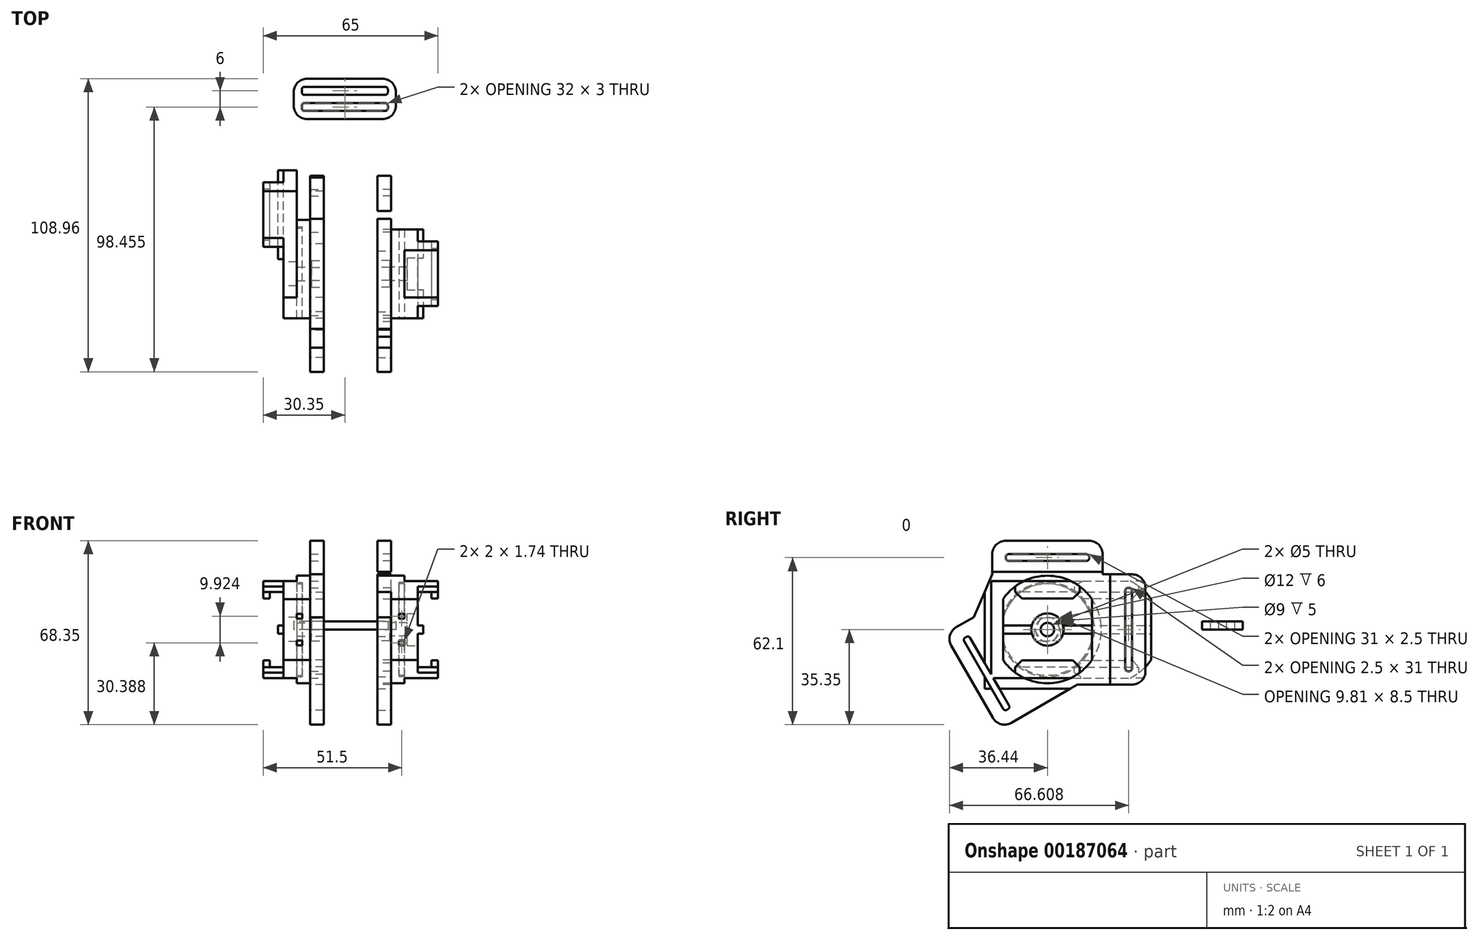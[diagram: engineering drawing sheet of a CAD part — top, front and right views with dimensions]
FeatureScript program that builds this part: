
annotation { "Feature Type Name" : "Feature", "Feature Type Description" : "" }
export const myFeature = defineFeature(function(context is Context, id is Id, definition is map)
    precondition{}
    {
        {
            var Q0;
            Q0=qCreatedBy(makeId("Right.planeOp"),FACE);
            var sketch = newSketch(context, id + "F0", { "sketchPlane" : qUnion([Q0])});
            skLineSegment(sketch, "E0", {"start": v(-29.5, 20.5) * mm, "end": v(-20.5, 20.5) * mm});
            skLineSegment(sketch, "E1", {"start": v(23.92, -34.5) * mm, "end": v(-4.88, -34.5) * mm});
            skLineSegment(sketch, "E2", {"start": v(-4.88, -34.5) * mm, "end": v(-6.94, -30.93) * mm});
            skLineSegment(sketch, "E3", {"start": v(-29.5, 8.15) * mm, "end": v(-29.5, 20.5) * mm});
            skLineSegment(sketch, "E4", {"start": v(-20.5, 20.5) * mm, "end": v(-20.5, 33) * mm});
            skLineSegment(sketch, "E5", {"start": v(-20.5, 33) * mm, "end": v(20.5, 33) * mm});
            skLineSegment(sketch, "E6", {"start": v(20.5, 33) * mm, "end": v(20.5, 20.5) * mm});
            skLineSegment(sketch, "E7", {"start": v(23.92, 20.5) * mm, "end": v(36.42, 20.5) * mm});
            skLineSegment(sketch, "E8", {"start": v(36.42, 20.5) * mm, "end": v(36.42, -20.5) * mm});
            skLineSegment(sketch, "E9", {"start": v(36.42, -20.5) * mm, "end": v(23.92, -20.5) * mm});
            skLineSegment(sketch, "E10", {"start": v(-27.44, 4.58) * mm, "end": v(-38.27, -1.67) * mm});
            skLineSegment(sketch, "E11", {"start": v(-17.77, -37.18) * mm, "end": v(-6.94, -30.93) * mm});
            skLineSegment(sketch, "E12.bottom", {"start": v(-15.5, 28) * mm, "end": v(15.5, 28) * mm});
            skLineSegment(sketch, "E12.top", {"start": v(-15.5, 25.5) * mm, "end": v(15.5, 25.5) * mm});
            skLineSegment(sketch, "E12.left", {"start": v(-15.5, 28) * mm, "end": v(-15.5, 25.5) * mm});
            skLineSegment(sketch, "E12.right", {"start": v(15.5, 28) * mm, "end": v(15.5, 25.5) * mm});
            skLineSegment(sketch, "E13.bottom", {"start": v(28.92, 15.5) * mm, "end": v(31.42, 15.5) * mm});
            skLineSegment(sketch, "E13.top", {"start": v(28.92, -15.5) * mm, "end": v(31.42, -15.5) * mm});
            skLineSegment(sketch, "E13.left", {"start": v(28.92, 15.5) * mm, "end": v(28.92, -15.5) * mm});
            skLineSegment(sketch, "E13.right", {"start": v(31.42, 15.5) * mm, "end": v(31.42, -15.5) * mm});
            skLineSegment(sketch, "E14", {"start": v(0, 28) * mm, "end": v(0, 33) * mm, "construction": true});
            skLineSegment(sketch, "E15", {"start": v(31.42, 0) * mm, "end": v(36.42, 0) * mm, "construction": true});
            skLineSegment(sketch, "E16", {"start": v(-38.27, -1.67) * mm, "end": v(-17.77, -37.18) * mm});
            skLineSegment(sketch, "E17", {"start": v(-31.44, -3.5) * mm, "end": v(-29.27, -2.25) * mm});
            skLineSegment(sketch, "E18", {"start": v(-29.27, -2.25) * mm, "end": v(-13.77, -29.1) * mm});
            skLineSegment(sketch, "E19", {"start": v(-13.77, -29.1) * mm, "end": v(-15.94, -30.35) * mm});
            skLineSegment(sketch, "E20", {"start": v(-15.94, -30.35) * mm, "end": v(-31.44, -3.5) * mm});
            skLineSegment(sketch, "E21", {"start": v(-23.69, -16.92) * mm, "end": v(-28.02, -19.42) * mm, "construction": true});
            skPoint(sketch, "E22.endSnap0", {"position": v(0, 25.5) * mm});
            skCircle(sketch, "E23", {"center": v(0, 0) * mm, "radius": 2.5 * mm});
            skCircle(sketch, "E24", {"center": v(0, 0) * mm, "radius": 20 * mm, "construction": true});
            skLineSegment(sketch, "E25.trimOffspring", {"start": v(23.92, -20.5) * mm, "end": v(23.92, -34.5) * mm});
            skLineSegment(sketch, "E26.trimOffspring", {"start": v(-27.44, 4.58) * mm, "end": v(-29.5, 8.15) * mm});
            skLineSegment(sketch, "E27.trimOffspring", {"start": v(20.5, 20.5) * mm, "end": v(23.92, 20.5) * mm});
            skLineSegment(sketch, "E28", {"start": v(0, 25.5) * mm, "end": v(0, 0) * mm, "construction": true});
            skLineSegment(sketch, "E29", {"start": v(0, 0) * mm, "end": v(31.42, 0) * mm, "construction": true});
            skSolve(sketch);
        }
        {
            var Q0;
            Q0=makeQuery(id+"F0.imprint","IMPRINT",FACE,{"disambiguationData":[TD([[makeQuery(id+"F0.imprint","IMPRINT",EDGE,{"derivedFrom":sQuery(id+"F0.wireOp",EDGE,"E0")}),-1.0]])]});
            extrude(context, id + "F1", {"entities" : qUnion([Q0]), "depth" : 5 * mm});
        }
        {
            var Q0;
            Q0=qCreatedBy(makeId("Front.planeOp"),FACE);
            var sketch = newSketch(context, id + "F2", { "sketchPlane" : qUnion([Q0])});
            skLineSegment(sketch, "E30", {"start": v(0, 0) * mm, "end": v(44.24, 0) * mm, "construction": true});
            skLineSegment(sketch, "E31", {"start": v(5, 2.5) * mm, "end": v(5, 20) * mm});
            skLineSegment(sketch, "E32", {"start": v(5, 20) * mm, "end": v(10, 20) * mm});
            skLineSegment(sketch, "E33", {"start": v(10, 20) * mm, "end": v(10, 17.5) * mm});
            skLineSegment(sketch, "E34", {"start": v(10, 17.5) * mm, "end": v(8, 17.5) * mm});
            skLineSegment(sketch, "E35", {"start": v(8, 17.5) * mm, "end": v(8, 2.5) * mm});
            skLineSegment(sketch, "E36", {"start": v(8, 2.5) * mm, "end": v(5, 2.5) * mm});
            skSolve(sketch);
        }
        {
            var Q0;
            Q0 = qSketchRegion(id + "F2", true);
            var Q1;
            Q1=sQuery(id+"F2.wireOp",EDGE,"E30");
            revolve(context, id + "F3", {"operationType" : NewBodyOperationType.ADD, "entities" : qUnion([Q0]), "axis" : qUnion([Q1]), "revolveType" : RevolveType.FULL});
        }
        {
            var Q0;
            Q0=makeQuery(id+"F1.opExtrude","CAP_FACE",FACE,{"disambiguationData":[OSD([sQuery(id+"F0.wireOp",EDGE,"E0"),sQuery(id+"F0.wireOp",EDGE,"OmQOhUAe-Qu7m-89W4-GLdg-3MtDFwY1XBf1"),sQuery(id+"F0.wireOp",EDGE,"E1"),sQuery(id+"F0.wireOp",EDGE,"E2"),sQuery(id+"F0.wireOp",EDGE,"E3"),sQuery(id+"F0.wireOp",EDGE,"E4"),sQuery(id+"F0.wireOp",EDGE,"E5"),sQuery(id+"F0.wireOp",EDGE,"E6"),sQuery(id+"F0.wireOp",EDGE,"E7"),sQuery(id+"F0.wireOp",EDGE,"E8"),sQuery(id+"F0.wireOp",EDGE,"E9"),sQuery(id+"F0.wireOp",EDGE,"E10"),sQuery(id+"F0.wireOp",EDGE,"E11"),sQuery(id+"F0.wireOp",EDGE,"E12.bottom"),sQuery(id+"F0.wireOp",EDGE,"E12.top"),sQuery(id+"F0.wireOp",EDGE,"E12.left"),sQuery(id+"F0.wireOp",EDGE,"E12.right"),sQuery(id+"F0.wireOp",EDGE,"E13.bottom"),sQuery(id+"F0.wireOp",EDGE,"E13.top"),sQuery(id+"F0.wireOp",EDGE,"E13.left"),sQuery(id+"F0.wireOp",EDGE,"E13.right"),sQuery(id+"F0.wireOp",EDGE,"E16"),sQuery(id+"F0.wireOp",EDGE,"E17"),sQuery(id+"F0.wireOp",EDGE,"E18"),sQuery(id+"F0.wireOp",EDGE,"E19"),sQuery(id+"F0.wireOp",EDGE,"E20"),sQuery(id+"F0.wireOp",EDGE,"E23"),sQuery(id+"F0.wireOp",EDGE,"E25.trimOffspring"),sQuery(id+"F0.wireOp",EDGE,"E26.trimOffspring"),sQuery(id+"F0.wireOp",EDGE,"E27.trimOffspring")])],"isStart":true});
            var sketch = newSketch(context, id + "F4", { "sketchPlane" : qUnion([Q0])});
            skCircle(sketch, "E37.cCircle", {"center": v(0, 0) * mm, "radius": 4.25 * mm, "construction": true});
            skLineSegment(sketch, "E37.0", {"start": v(2.45, 4.25) * mm, "end": v(4.9, 0) * mm});
            skLineSegment(sketch, "E37.1", {"start": v(4.9, 0) * mm, "end": v(2.45, -4.25) * mm});
            skLineSegment(sketch, "E37.2", {"start": v(2.45, -4.25) * mm, "end": v(-2.45, -4.25) * mm});
            skLineSegment(sketch, "E37.3", {"start": v(-2.45, -4.25) * mm, "end": v(-4.9, 0) * mm});
            skLineSegment(sketch, "E37.4", {"start": v(-4.9, 0) * mm, "end": v(-2.45, 4.25) * mm});
            skLineSegment(sketch, "E37.5", {"start": v(-2.45, 4.25) * mm, "end": v(2.45, 4.25) * mm});
            skPoint(sketch, "E37.0.midPoint", {"position": v(3.68, 2.12) * mm});
            skSolve(sketch);
        }
        {
            var Q0;
            Q0 = qSketchRegion(id + "F4", true);
            extrude(context, id + "F5", {"entities" : qUnion([Q0]), "operationType" : NewBodyOperationType.REMOVE, "oppositeDirection" : true, "depth" : 4.5 * mm});
        }
        {
            var Q0;
            Q0=makeQuery(id+"F1.opExtrude","CAP_FACE",FACE,{"disambiguationData":[OSD([sQuery(id+"F0.wireOp",EDGE,"E0"),sQuery(id+"F0.wireOp",EDGE,"E1"),sQuery(id+"F0.wireOp",EDGE,"E2"),sQuery(id+"F0.wireOp",EDGE,"E3"),sQuery(id+"F0.wireOp",EDGE,"E4"),sQuery(id+"F0.wireOp",EDGE,"E5"),sQuery(id+"F0.wireOp",EDGE,"E6"),sQuery(id+"F0.wireOp",EDGE,"E7"),sQuery(id+"F0.wireOp",EDGE,"E8"),sQuery(id+"F0.wireOp",EDGE,"E9"),sQuery(id+"F0.wireOp",EDGE,"E10"),sQuery(id+"F0.wireOp",EDGE,"E11"),sQuery(id+"F0.wireOp",EDGE,"E12.bottom"),sQuery(id+"F0.wireOp",EDGE,"E12.top"),sQuery(id+"F0.wireOp",EDGE,"E12.left"),sQuery(id+"F0.wireOp",EDGE,"E12.right"),sQuery(id+"F0.wireOp",EDGE,"E13.bottom"),sQuery(id+"F0.wireOp",EDGE,"E13.top"),sQuery(id+"F0.wireOp",EDGE,"E13.left"),sQuery(id+"F0.wireOp",EDGE,"E13.right"),sQuery(id+"F0.wireOp",EDGE,"E16"),sQuery(id+"F0.wireOp",EDGE,"E17"),sQuery(id+"F0.wireOp",EDGE,"E18"),sQuery(id+"F0.wireOp",EDGE,"E19"),sQuery(id+"F0.wireOp",EDGE,"E20"),sQuery(id+"F0.wireOp",EDGE,"E23"),sQuery(id+"F0.wireOp",EDGE,"E25.trimOffspring"),sQuery(id+"F0.wireOp",EDGE,"E26.trimOffspring"),sQuery(id+"F0.wireOp",EDGE,"E27.trimOffspring")])],"isStart":false});
            var sketch = newSketch(context, id + "F6", { "sketchPlane" : qUnion([Q0])});
            skLineSegment(sketch, "E38", {"start": v(-20.5, 20.5) * mm, "end": v(-27.44, 4.58) * mm});
            skLineSegment(sketch, "E39.0", {"start": v(-29.5, 20.5) * mm, "end": v(-20.5, 20.5) * mm});
            skLineSegment(sketch, "E40.0", {"start": v(-29.5, 8.15) * mm, "end": v(-29.5, 20.5) * mm});
            skPoint(sketch, "E41.0", {"position": v(-28.47, 6.36) * mm});
            skLineSegment(sketch, "E42", {"start": v(23.92, -20.5) * mm, "end": v(11.12, -20.5) * mm});
            skLineSegment(sketch, "E43", {"start": v(-6.94, -30.93) * mm, "end": v(11.12, -20.5) * mm});
            skLineSegment(sketch, "E44.0", {"start": v(23.92, -20.5) * mm, "end": v(23.92, -34.5) * mm});
            skLineSegment(sketch, "E45.0", {"start": v(23.92, -34.5) * mm, "end": v(-4.88, -34.5) * mm});
            skLineSegment(sketch, "E46.0", {"start": v(-4.88, -34.5) * mm, "end": v(-6.94, -30.93) * mm});
            skSolve(sketch);
        }
        {
            var Q0;
            Q0 = qSketchRegion(id + "F6", true);
            var Q1;
            Q1=makeQuery(id+"F6.imprint","IMPRINT",FACE,{"disambiguationData":[TD([[makeQuery(id+"F6.imprint","IMPRINT",EDGE,{"derivedFrom":sQuery(id+"F6.wireOp",EDGE,"E38")}),-1.0]])]});
            extrude(context, id + "F7", {"entities" : qUnion([Q0, Q1]), "operationType" : NewBodyOperationType.REMOVE, "oppositeDirection" : true, "depth" : 25 * mm});
        }
        {
            var Q0;
            Q0=makeQuery(id+"F1.opExtrude","SWEPT_EDGE",EDGE,{"disambiguationData":[OSD([sQuery(id+"F0.wireOp",EDGE,"E12.bottom"),sQuery(id+"F0.wireOp",EDGE,"E12.left")])]});
            var Q1;
            Q1=makeQuery(id+"F1.opExtrude","SWEPT_EDGE",EDGE,{"disambiguationData":[OSD([sQuery(id+"F0.wireOp",EDGE,"E12.bottom"),sQuery(id+"F0.wireOp",EDGE,"E12.right")])]});
            var Q2;
            Q2=makeQuery(id+"F1.opExtrude","SWEPT_EDGE",EDGE,{"disambiguationData":[OSD([sQuery(id+"F0.wireOp",EDGE,"E12.top"),sQuery(id+"F0.wireOp",EDGE,"E12.right")])]});
            var Q3;
            Q3=makeQuery(id+"F1.opExtrude","SWEPT_EDGE",EDGE,{"disambiguationData":[OSD([sQuery(id+"F0.wireOp",EDGE,"E12.top"),sQuery(id+"F0.wireOp",EDGE,"E12.left")])]});
            var Q4;
            Q4=makeQuery(id+"F1.opExtrude","SWEPT_EDGE",EDGE,{"disambiguationData":[OSD([sQuery(id+"F0.wireOp",EDGE,"E13.bottom"),sQuery(id+"F0.wireOp",EDGE,"E13.right")])]});
            var Q5;
            Q5=makeQuery(id+"F1.opExtrude","SWEPT_EDGE",EDGE,{"disambiguationData":[OSD([sQuery(id+"F0.wireOp",EDGE,"E13.bottom"),sQuery(id+"F0.wireOp",EDGE,"E13.left")])]});
            var Q6;
            Q6=makeQuery(id+"F1.opExtrude","SWEPT_EDGE",EDGE,{"disambiguationData":[OSD([sQuery(id+"F0.wireOp",EDGE,"E13.top"),sQuery(id+"F0.wireOp",EDGE,"E13.right")])]});
            var Q7;
            Q7=makeQuery(id+"F1.opExtrude","SWEPT_EDGE",EDGE,{"disambiguationData":[OSD([sQuery(id+"F0.wireOp",EDGE,"E13.top"),sQuery(id+"F0.wireOp",EDGE,"E13.left")])]});
            var Q8;
            Q8=makeQuery(id+"F1.opExtrude","SWEPT_EDGE",EDGE,{"disambiguationData":[OSD([sQuery(id+"F0.wireOp",EDGE,"E18"),sQuery(id+"F0.wireOp",EDGE,"E19")])]});
            var Q9;
            Q9=makeQuery(id+"F1.opExtrude","SWEPT_EDGE",EDGE,{"disambiguationData":[OSD([sQuery(id+"F0.wireOp",EDGE,"E19"),sQuery(id+"F0.wireOp",EDGE,"E20")])]});
            var Q10;
            Q10=makeQuery(id+"F1.opExtrude","SWEPT_EDGE",EDGE,{"disambiguationData":[OSD([sQuery(id+"F0.wireOp",EDGE,"E17"),sQuery(id+"F0.wireOp",EDGE,"E18")])]});
            var Q11;
            Q11=makeQuery(id+"F1.opExtrude","SWEPT_EDGE",EDGE,{"disambiguationData":[OSD([sQuery(id+"F0.wireOp",EDGE,"E17"),sQuery(id+"F0.wireOp",EDGE,"E20")])]});
            fillet(context, id + "F8", {"entities" : qUnion([Q0, Q1, Q2, Q3, Q4, Q5, Q6, Q7, Q8, Q9, Q10, Q11]), "radius" : 1 * mm, "tangentPropagation" : true, "allowEdgeOverflow" : false});
        }
        {
            var Q0;
            Q0=makeQuery(id+"F1.opExtrude","SWEPT_EDGE",EDGE,{"disambiguationData":[OSD([sQuery(id+"F0.wireOp",EDGE,"E4"),sQuery(id+"F0.wireOp",EDGE,"E5")])]});
            var Q1;
            Q1=makeQuery(id+"F1.opExtrude","SWEPT_EDGE",EDGE,{"disambiguationData":[OSD([sQuery(id+"F0.wireOp",EDGE,"E5"),sQuery(id+"F0.wireOp",EDGE,"E6")])]});
            var Q2;
            Q2=makeQuery(id+"F1.opExtrude","SWEPT_EDGE",EDGE,{"disambiguationData":[OSD([sQuery(id+"F0.wireOp",EDGE,"E7"),sQuery(id+"F0.wireOp",EDGE,"E8")])]});
            var Q3;
            Q3=makeQuery(id+"F1.opExtrude","SWEPT_EDGE",EDGE,{"disambiguationData":[OSD([sQuery(id+"F0.wireOp",EDGE,"E8"),sQuery(id+"F0.wireOp",EDGE,"E9")])]});
            var Q4;
            Q4=makeQuery(id+"F1.opExtrude","SWEPT_EDGE",EDGE,{"disambiguationData":[OSD([sQuery(id+"F0.wireOp",EDGE,"E10"),sQuery(id+"F0.wireOp",EDGE,"E16")])]});
            var Q5;
            Q5=makeQuery(id+"F1.opExtrude","SWEPT_EDGE",EDGE,{"disambiguationData":[OSD([sQuery(id+"F0.wireOp",EDGE,"E11"),sQuery(id+"F0.wireOp",EDGE,"E16")])]});
            fillet(context, id + "F9", {"entities" : qUnion([Q0, Q1, Q2, Q3, Q4, Q5]), "radius" : 5 * mm, "tangentPropagation" : true, "allowEdgeOverflow" : false});
        }
        {
            var Q0;
            Q0=qCreatedBy(makeId("Right.planeOp"),FACE);
            cPlane(context, id + "F10", {"entities" : qUnion([Q0]), "cplaneType" : CPlaneType.OFFSET, "offset" : 10 * mm, "oppositeDirection" : true, "width" : 150 * mm, "height" : 150 * mm});
        }
        {
            var Q0;
            Q0=makeQuery(id+"F1.opExtrude","SWEPT_BODY",BODY,{"disambiguationData":[OSD([sQuery(id+"F0.wireOp",EDGE,"E0"),sQuery(id+"F0.wireOp",EDGE,"E1"),sQuery(id+"F0.wireOp",EDGE,"E2"),sQuery(id+"F0.wireOp",EDGE,"E3"),sQuery(id+"F0.wireOp",EDGE,"E4"),sQuery(id+"F0.wireOp",EDGE,"E5"),sQuery(id+"F0.wireOp",EDGE,"E6"),sQuery(id+"F0.wireOp",EDGE,"E7"),sQuery(id+"F0.wireOp",EDGE,"E8"),sQuery(id+"F0.wireOp",EDGE,"E9"),sQuery(id+"F0.wireOp",EDGE,"E10"),sQuery(id+"F0.wireOp",EDGE,"E11"),sQuery(id+"F0.wireOp",EDGE,"E12.bottom"),sQuery(id+"F0.wireOp",EDGE,"E12.top"),sQuery(id+"F0.wireOp",EDGE,"E12.left"),sQuery(id+"F0.wireOp",EDGE,"E12.right"),sQuery(id+"F0.wireOp",EDGE,"E13.bottom"),sQuery(id+"F0.wireOp",EDGE,"E13.top"),sQuery(id+"F0.wireOp",EDGE,"E13.left"),sQuery(id+"F0.wireOp",EDGE,"E13.right"),sQuery(id+"F0.wireOp",EDGE,"E16"),sQuery(id+"F0.wireOp",EDGE,"E17"),sQuery(id+"F0.wireOp",EDGE,"E18"),sQuery(id+"F0.wireOp",EDGE,"E19"),sQuery(id+"F0.wireOp",EDGE,"E20"),sQuery(id+"F0.wireOp",EDGE,"E23"),sQuery(id+"F0.wireOp",EDGE,"E25.trimOffspring"),sQuery(id+"F0.wireOp",EDGE,"E26.trimOffspring"),sQuery(id+"F0.wireOp",EDGE,"E27.trimOffspring")])]});
            var Q1;
            Q1=qCreatedBy(id+"F10.planeOp",FACE);
            mirror(context, id + "F11", {"entities" : qUnion([Q0]), "mirrorPlane" : qUnion([Q1])});
        }
        {
            var Q0;
            Q0=makeQuery(id+"F3.opRevolve","SWEPT_FACE",FACE,{"disambiguationData":[OSD([sQuery(id+"F2.wireOp",EDGE,"E35")])]});
            var sketch = newSketch(context, id + "F12", { "sketchPlane" : qUnion([Q0])});
            skCircle(sketch, "E47", {"center": v(0, 0) * mm, "radius": 17 * mm});
            skPoint(sketch, "E48", {"position": v(0, 17.5) * mm});
            skCircle(sketch, "E49", {"center": v(0, 0) * mm, "radius": 2.5 * mm});
            skSolve(sketch);
        }
        {
            var Q0;
            Q0 = qSketchRegion(id + "F12", true);
            extrude(context, id + "F13", {"entities" : qUnion([Q0]), "depth" : 2 * mm});
        }
        {
            var Q0;
            Q0=makeQuery(id+"F13.opExtrude","CAP_FACE",FACE,{"disambiguationData":[OSD([sQuery(id+"F12.wireOp",EDGE,"E47"),sQuery(id+"F12.wireOp",EDGE,"E49")])],"isStart":false});
            var sketch = newSketch(context, id + "F14", { "sketchPlane" : qUnion([Q0])});
            skLineSegment(sketch, "E50", {"start": v(-16.5, 18) * mm, "end": v(16.5, 18) * mm});
            skLineSegment(sketch, "E51", {"start": v(16.5, 18) * mm, "end": v(16.5, -18) * mm});
            skLineSegment(sketch, "E52", {"start": v(16.5, -18) * mm, "end": v(-16.5, -18) * mm});
            skLineSegment(sketch, "E53", {"start": v(-16.5, -18) * mm, "end": v(-16.5, 18) * mm});
            skLineSegment(sketch, "E54", {"start": v(0, 0) * mm, "end": v(0, 18) * mm, "construction": true});
            skLineSegment(sketch, "E55", {"start": v(0, 0) * mm, "end": v(-16.5, 0) * mm, "construction": true});
            skCircle(sketch, "E56.0", {"center": v(0, 0) * mm, "radius": 2.5 * mm});
            skSolve(sketch);
        }
        {
            var Q0;
            Q0 = qSketchRegion(id + "F14", true);
            extrude(context, id + "F15", {"entities" : qUnion([Q0]), "operationType" : NewBodyOperationType.ADD, "depth" : 5 * mm});
        }
        {
            var Q0;
            Q0=makeQuery(id+"F15.opExtrude","SWEPT_FACE",FACE,{"disambiguationData":[OSD([sQuery(id+"F14.wireOp",EDGE,"E53")])]});
            var sketch = newSketch(context, id + "F16", { "sketchPlane" : qUnion([Q0])});
            skLineSegment(sketch, "E57", {"start": v(15, 0) * mm, "end": v(17, 0) * mm, "construction": true});
            skPoint(sketch, "E57.endSnap0", {"position": v(15, 0) * mm});
            skLineSegment(sketch, "E58", {"start": v(17, 0) * mm, "end": v(17, 1.5) * mm});
            skLineSegment(sketch, "E59", {"start": v(17, 1.5) * mm, "end": v(15, 1.5) * mm});
            skLineSegment(sketch, "E60", {"start": v(15, 1.5) * mm, "end": v(15, 0) * mm});
            skLineSegment(sketch, "E61", {"start": v(15, 14) * mm, "end": v(20, 14) * mm});
            skLineSegment(sketch, "E62", {"start": v(20, 14) * mm, "end": v(20, 11.5) * mm});
            skLineSegment(sketch, "E63", {"start": v(20, 11.5) * mm, "end": v(22.5, 11.5) * mm});
            skLineSegment(sketch, "E64", {"start": v(22.5, 11.5) * mm, "end": v(22.5, 18) * mm});
            skLineSegment(sketch, "E65", {"start": v(22.5, 18) * mm, "end": v(15, 18) * mm});
            skLineSegment(sketch, "E66", {"start": v(15, 18) * mm, "end": v(15, 14) * mm});
            skLineSegment(sketch, "E67.MirrorCS", {"start": v(22.5, -18) * mm, "end": v(15, -18) * mm});
            skLineSegment(sketch, "E68.MirrorCS", {"start": v(22.5, -11.5) * mm, "end": v(22.5, -18) * mm});
            skLineSegment(sketch, "E69.MirrorCS", {"start": v(15, -18) * mm, "end": v(15, -14) * mm});
            skLineSegment(sketch, "E70.MirrorCS", {"start": v(15, -14) * mm, "end": v(20, -14) * mm});
            skLineSegment(sketch, "E71.MirrorCS", {"start": v(20, -14) * mm, "end": v(20, -11.5) * mm});
            skLineSegment(sketch, "E72.MirrorCS", {"start": v(20, -11.5) * mm, "end": v(22.5, -11.5) * mm});
            skLineSegment(sketch, "E73.MirrorCS", {"start": v(17, -1.5) * mm, "end": v(15, -1.5) * mm});
            skLineSegment(sketch, "E74.MirrorCS", {"start": v(17, 0) * mm, "end": v(17, -1.5) * mm});
            skLineSegment(sketch, "E75.MirrorCS", {"start": v(15, -1.5) * mm, "end": v(15, 0) * mm});
            skSolve(sketch);
        }
        {
            var Q0;
            Q0 = qSketchRegion(id + "F16", true);
            var Q1;
            Q1=makeQuery(id+"F15.opExtrude","SWEPT_FACE",FACE,{"disambiguationData":[OSD([sQuery(id+"F14.wireOp",EDGE,"E51")])]});
            extrude(context, id + "F17", {"entities" : qUnion([Q0]), "operationType" : NewBodyOperationType.ADD, "endBound" : BoundingType.UP_TO_SURFACE, "oppositeDirection" : true, "endBoundEntityFace" : qUnion([Q1]), "depth" : 25 * mm});
        }
        {
            var Q0;
            Q0=makeQuery(id+"F17.opExtrude","SWEPT_FACE",FACE,{"disambiguationData":[OSD([sQuery(id+"F16.wireOp",EDGE,"E64")])]});
            var sketch = newSketch(context, id + "F18", { "sketchPlane" : qUnion([Q0])});
            skLineSegment(sketch, "E76", {"start": v(0, 11.5) * mm, "end": v(0, 0) * mm, "construction": true});
            skLineSegment(sketch, "E77", {"start": v(9.5, 11.5) * mm, "end": v(12, 14) * mm});
            skLineSegment(sketch, "E78", {"start": v(12, 14) * mm, "end": v(12, 18) * mm});
            skLineSegment(sketch, "E79", {"start": v(12, 18) * mm, "end": v(0, 18) * mm});
            skLineSegment(sketch, "E80", {"start": v(0, 18) * mm, "end": v(0, 23.18) * mm, "construction": true});
            skLineSegment(sketch, "E81", {"start": v(0, 23.18) * mm, "end": v(19.25, 23.18) * mm});
            skLineSegment(sketch, "E82", {"start": v(19.25, 23.18) * mm, "end": v(19.25, 11.5) * mm});
            skLineSegment(sketch, "E83", {"start": v(19.25, 11.5) * mm, "end": v(9.5, 11.5) * mm});
            skLineSegment(sketch, "E84", {"start": v(0, 0) * mm, "end": v(16.5, 0) * mm, "construction": true});
            skLineSegment(sketch, "E85.MirrorCS", {"start": v(0, 23.18) * mm, "end": v(-19.25, 23.18) * mm});
            skLineSegment(sketch, "E86.MirrorCS", {"start": v(-12, 18) * mm, "end": v(0, 18) * mm});
            skLineSegment(sketch, "E87.MirrorCS", {"start": v(-12, 14) * mm, "end": v(-12, 18) * mm});
            skLineSegment(sketch, "E88.MirrorCS", {"start": v(-9.5, 11.5) * mm, "end": v(-12, 14) * mm});
            skLineSegment(sketch, "E89.MirrorCS", {"start": v(-19.25, 11.5) * mm, "end": v(-9.5, 11.5) * mm});
            skLineSegment(sketch, "E90.MirrorCS", {"start": v(-19.25, 23.18) * mm, "end": v(-19.25, 11.5) * mm});
            skLineSegment(sketch, "E91.MirrorCS", {"start": v(-19.25, -23.18) * mm, "end": v(-19.25, -11.5) * mm});
            skLineSegment(sketch, "E92.MirrorCS", {"start": v(0, -23.18) * mm, "end": v(-19.25, -23.18) * mm});
            skLineSegment(sketch, "E93.MirrorCS", {"start": v(0, -23.18) * mm, "end": v(19.25, -23.18) * mm});
            skLineSegment(sketch, "E94.MirrorCS", {"start": v(19.25, -23.18) * mm, "end": v(19.25, -11.5) * mm});
            skLineSegment(sketch, "E95.MirrorCS", {"start": v(19.25, -11.5) * mm, "end": v(9.5, -11.5) * mm});
            skLineSegment(sketch, "E96.MirrorCS", {"start": v(9.5, -11.5) * mm, "end": v(12, -14) * mm});
            skLineSegment(sketch, "E97.MirrorCS", {"start": v(12, -14) * mm, "end": v(12, -18) * mm});
            skLineSegment(sketch, "E98.MirrorCS", {"start": v(12, -18) * mm, "end": v(0, -18) * mm});
            skLineSegment(sketch, "E99.MirrorCS", {"start": v(-12, -18) * mm, "end": v(0, -18) * mm});
            skLineSegment(sketch, "E100.MirrorCS", {"start": v(-12, -14) * mm, "end": v(-12, -18) * mm});
            skLineSegment(sketch, "E101.MirrorCS", {"start": v(-9.5, -11.5) * mm, "end": v(-12, -14) * mm});
            skLineSegment(sketch, "E102.MirrorCS", {"start": v(-19.25, -11.5) * mm, "end": v(-9.5, -11.5) * mm});
            skSolve(sketch);
        }
        {
            var Q0;
            Q0 = qSketchRegion(id + "F18", true);
            var Q1;
            {var subQ8=sQuery(id+"F16.wireOp",EDGE,"E59");var subQ12=sQuery(id+"F14.wireOp",EDGE,"E53");var subQ19=sQuery(id+"F14.wireOp",EDGE,"E51");var subQ20=sQuery(id+"F14.wireOp",EDGE,"E56.0");Q1=makeQuery(id+"F17.boolean.opBoolean","SPLIT",FACE,{"disambiguationData":[TD([makeQuery(id+"F17.opExtrude","SWEPT_FACE",FACE,{"disambiguationData":[OSD([subQ8])]})])],"derivedFrom":makeQuery(id+"F15.opExtrude","CAP_FACE",FACE,{"disambiguationData":[OSD([sQuery(id+"F14.wireOp",EDGE,"E50"),subQ19,sQuery(id+"F14.wireOp",EDGE,"E52"),subQ12,subQ20])],"isStart":false})});}
            extrude(context, id + "F19", {"entities" : qUnion([Q0]), "operationType" : NewBodyOperationType.REMOVE, "endBound" : BoundingType.UP_TO_SURFACE, "oppositeDirection" : true, "endBoundEntityFace" : qUnion([Q1]), "depth" : 25 * mm});
        }
        {
            var Q0;
            {var subQ8=sQuery(id+"F16.wireOp",EDGE,"E59");var subQ12=sQuery(id+"F14.wireOp",EDGE,"E53");var subQ19=sQuery(id+"F14.wireOp",EDGE,"E51");var subQ20=sQuery(id+"F14.wireOp",EDGE,"E56.0");Q0=makeQuery(id+"F19.boolean.opBoolean","MERGE",FACE,{"derivedFrom":[makeQuery(id+"F17.boolean.opBoolean","SPLIT",FACE,{"disambiguationData":[TD([makeQuery(id+"F17.opExtrude","SWEPT_FACE",FACE,{"disambiguationData":[OSD([subQ8])]})])],"derivedFrom":makeQuery(id+"F15.opExtrude","CAP_FACE",FACE,{"disambiguationData":[OSD([sQuery(id+"F14.wireOp",EDGE,"E50"),subQ19,sQuery(id+"F14.wireOp",EDGE,"E52"),subQ12,subQ20])],"isStart":false})})],"fromTools":[makeQuery(id+"F19.opExtrude","CAP_FACE",FACE,{"disambiguationData":[OSD([sQuery(id+"F18.wireOp",EDGE,"E77"),sQuery(id+"F18.wireOp",EDGE,"E78"),sQuery(id+"F18.wireOp",EDGE,"E79"),sQuery(id+"F18.wireOp",EDGE,"E81"),sQuery(id+"F18.wireOp",EDGE,"E82"),sQuery(id+"F18.wireOp",EDGE,"E83"),sQuery(id+"F18.wireOp",EDGE,"E85.MirrorCS"),sQuery(id+"F18.wireOp",EDGE,"E86.MirrorCS"),sQuery(id+"F18.wireOp",EDGE,"E87.MirrorCS"),sQuery(id+"F18.wireOp",EDGE,"E88.MirrorCS"),sQuery(id+"F18.wireOp",EDGE,"E89.MirrorCS"),sQuery(id+"F18.wireOp",EDGE,"E90.MirrorCS")])],"isStart":false})]});}
            var sketch = newSketch(context, id + "F20", { "sketchPlane" : qUnion([Q0])});
            skCircle(sketch, "E103", {"center": v(0, 0) * mm, "radius": 6 * mm});
            skSolve(sketch);
        }
        {
            var Q0;
            Q0 = qSketchRegion(id + "F20", true);
            extrude(context, id + "F21", {"entities" : qUnion([Q0]), "operationType" : NewBodyOperationType.REMOVE, "oppositeDirection" : true, "depth" : 4 * mm, "hasSecondDirection" : true, "secondDirectionOppositeDirection" : false, "secondDirectionDepth" : 5 * mm});
        }
        {
            var Q0;
            {var subQ0=sQuery(id+"F14.wireOp",EDGE,"E51");var subQ1=sQuery(id+"F14.wireOp",EDGE,"E50");var subQ3=sQuery(id+"F14.wireOp",EDGE,"E53");Q0=makeQuery(id+"F15.boolean.opBoolean","SPLIT",FACE,{"disambiguationData":[TD([makeQuery(id+"F15.opExtrude","SWEPT_FACE",FACE,{"disambiguationData":[OSD([subQ1])]})])],"derivedFrom":makeQuery(id+"F15.opExtrude","CAP_FACE",FACE,{"disambiguationData":[OSD([subQ1,subQ0,sQuery(id+"F14.wireOp",EDGE,"E52"),subQ3,sQuery(id+"F14.wireOp",EDGE,"E56.0")])],"isStart":true})});}
            var sketch = newSketch(context, id + "F22", { "sketchPlane" : qUnion([Q0])});
            skArc(sketch, "E104.0", {"start": v(-16.5, -11.3) * mm, "mid": v(0, -20) * mm, "end": v(16.5, -11.3) * mm});
            skLineSegment(sketch, "E105", {"start": v(0, 21.5) * mm, "end": v(23.34, 21.5) * mm});
            skPoint(sketch, "E105.startSnap0", {"position": v(0, 17) * mm});
            skLineSegment(sketch, "E106", {"start": v(23.34, 21.5) * mm, "end": v(23.34, -22.05) * mm});
            skLineSegment(sketch, "E107", {"start": v(23.34, -22.05) * mm, "end": v(0, -22.05) * mm});
            skLineSegment(sketch, "E108", {"start": v(0, 21.5) * mm, "end": v(0, -22.05) * mm, "construction": true});
            skLineSegment(sketch, "E109.MirrorCS", {"start": v(0, 21.5) * mm, "end": v(-23.34, 21.5) * mm});
            skLineSegment(sketch, "E110.MirrorCS", {"start": v(-23.34, 21.5) * mm, "end": v(-23.34, -22.05) * mm});
            skLineSegment(sketch, "E111.MirrorCS", {"start": v(-23.34, -22.05) * mm, "end": v(0, -22.05) * mm});
            skLineSegment(sketch, "E112", {"start": v(-16.5, 11.3) * mm, "end": v(-16.5, -11.3) * mm});
            skLineSegment(sketch, "E113", {"start": v(16.5, 11.3) * mm, "end": v(16.5, -11.3) * mm});
            skArc(sketch, "E114.trimOffspring", {"start": v(16.5, 11.3) * mm, "mid": v(0, 20) * mm, "end": v(-16.5, 11.3) * mm});
            skSolve(sketch);
        }
        {
            var Q0;
            Q0 = qSketchRegion(id + "F22", true);
            extrude(context, id + "F23", {"entities" : qUnion([Q0]), "operationType" : NewBodyOperationType.REMOVE, "oppositeDirection" : true, "depth" : 25 * mm, "hasSecondDirection" : true, "secondDirectionOppositeDirection" : false, "secondDirectionDepth" : 25 * mm});
        }
        {
            var Q0;
            Q0=makeQuery(id+"F11.opPattern","COPY",FACE,{"derivedFrom":makeQuery(id+"F3.opRevolve","SWEPT_FACE",FACE,{"disambiguationData":[OSD([sQuery(id+"F2.wireOp",EDGE,"E35")])]}),"instanceName":"1"});
            var sketch = newSketch(context, id + "F24", { "sketchPlane" : qUnion([Q0])});
            skCircle(sketch, "E115.0", {"center": v(0, 0) * mm, "radius": 2.5 * mm});
            skCircle(sketch, "E116", {"center": v(0, 0) * mm, "radius": 17 * mm});
            skPoint(sketch, "E117", {"position": v(0, 17.5) * mm});
            skPoint(sketch, "E118", {"position": v(0, 17) * mm});
            skSolve(sketch);
        }
        {
            var Q0;
            Q0 = qSketchRegion(id + "F24", true);
            extrude(context, id + "F25", {"entities" : qUnion([Q0]), "depth" : 2 * mm});
        }
        {
            var Q0;
            Q0=makeQuery(id+"F25.opExtrude","CAP_FACE",FACE,{"disambiguationData":[OSD([sQuery(id+"F24.wireOp",EDGE,"E115.0"),sQuery(id+"F24.wireOp",EDGE,"E116")])],"isStart":false});
            var sketch = newSketch(context, id + "F26", { "sketchPlane" : qUnion([Q0])});
            skLineSegment(sketch, "E119.bottom", {"start": v(16.5, 18) * mm, "end": v(-38.5, 18) * mm});
            skLineSegment(sketch, "E119.top", {"start": v(16.5, -18) * mm, "end": v(-38.5, -18) * mm});
            skLineSegment(sketch, "E119.left", {"start": v(16.5, 18) * mm, "end": v(16.5, -18) * mm});
            skLineSegment(sketch, "E119.right", {"start": v(-38.5, 18) * mm, "end": v(-38.5, -18) * mm});
            skPoint(sketch, "E119.middle", {"position": v(-11, 0) * mm});
            skCircle(sketch, "E120.0", {"center": v(0, 0) * mm, "radius": 2.5 * mm});
            skSolve(sketch);
        }
        {
            var Q0;
            Q0 = qSketchRegion(id + "F26", true);
            extrude(context, id + "F27", {"entities" : qUnion([Q0]), "operationType" : NewBodyOperationType.ADD, "depth" : 5 * mm});
        }
        {
            var Q0;
            Q0=makeQuery(id+"F27.opExtrude","SWEPT_FACE",FACE,{"disambiguationData":[OSD([sQuery(id+"F26.wireOp",EDGE,"E119.right")])]});
            var sketch = newSketch(context, id + "F28", { "sketchPlane" : qUnion([Q0])});
            skLineSegment(sketch, "E121", {"start": v(35, 0) * mm, "end": v(37, 0) * mm, "construction": true});
            skLineSegment(sketch, "E122", {"start": v(37, 0) * mm, "end": v(37, 1.5) * mm});
            skLineSegment(sketch, "E123", {"start": v(37, 1.5) * mm, "end": v(35, 1.5) * mm});
            skLineSegment(sketch, "E124", {"start": v(35, 1.5) * mm, "end": v(35, 0) * mm});
            skLineSegment(sketch, "E125", {"start": v(35, 14) * mm, "end": v(40, 14) * mm});
            skLineSegment(sketch, "E126", {"start": v(40, 14) * mm, "end": v(40, 11.5) * mm});
            skLineSegment(sketch, "E127", {"start": v(40, 11.5) * mm, "end": v(42.5, 11.5) * mm});
            skLineSegment(sketch, "E128", {"start": v(42.5, 11.5) * mm, "end": v(42.5, 18) * mm});
            skLineSegment(sketch, "E129", {"start": v(42.5, 18) * mm, "end": v(35, 18) * mm});
            skLineSegment(sketch, "E130", {"start": v(35, 18) * mm, "end": v(35, 14) * mm});
            skLineSegment(sketch, "E131.MirrorCS", {"start": v(37, 0) * mm, "end": v(37, -1.5) * mm});
            skLineSegment(sketch, "E132.MirrorCS", {"start": v(35, -1.5) * mm, "end": v(35, 0) * mm});
            skLineSegment(sketch, "E133.MirrorCS", {"start": v(35, -18) * mm, "end": v(35, -14) * mm});
            skLineSegment(sketch, "E134.MirrorCS", {"start": v(37, -1.5) * mm, "end": v(35, -1.5) * mm});
            skLineSegment(sketch, "E135.MirrorCS", {"start": v(42.5, -18) * mm, "end": v(35, -18) * mm});
            skLineSegment(sketch, "E136.MirrorCS", {"start": v(35, -14) * mm, "end": v(40, -14) * mm});
            skLineSegment(sketch, "E137.MirrorCS", {"start": v(42.5, -11.5) * mm, "end": v(42.5, -18) * mm});
            skLineSegment(sketch, "E138.MirrorCS", {"start": v(40, -14) * mm, "end": v(40, -11.5) * mm});
            skLineSegment(sketch, "E139.MirrorCS", {"start": v(40, -11.5) * mm, "end": v(42.5, -11.5) * mm});
            skSolve(sketch);
        }
        {
            var Q0;
            Q0 = qSketchRegion(id + "F28", true);
            extrude(context, id + "F29", {"entities" : qUnion([Q0]), "operationType" : NewBodyOperationType.ADD, "oppositeDirection" : true, "depth" : 33 * mm});
        }
        {
            var Q0;
            Q0=makeQuery(id+"F29.opExtrude","SWEPT_FACE",FACE,{"disambiguationData":[OSD([sQuery(id+"F28.wireOp",EDGE,"E128")])]});
            var sketch = newSketch(context, id + "F30", { "sketchPlane" : qUnion([Q0])});
            skLineSegment(sketch, "E140", {"start": v(-22, 11.5) * mm, "end": v(-12.5, 11.5) * mm, "construction": true});
            skLineSegment(sketch, "E141", {"start": v(-12.5, 11.5) * mm, "end": v(-10, 14) * mm});
            skLineSegment(sketch, "E142", {"start": v(-10, 14) * mm, "end": v(-10, 18) * mm});
            skLineSegment(sketch, "E143", {"start": v(-10, 18) * mm, "end": v(-5.5, 18) * mm});
            skLineSegment(sketch, "E144", {"start": v(-5.5, 18) * mm, "end": v(-5.5, 11.5) * mm});
            skLineSegment(sketch, "E145", {"start": v(-5.5, 11.5) * mm, "end": v(-12.5, 11.5) * mm});
            skLineSegment(sketch, "E146", {"start": v(-22, 11.5) * mm, "end": v(-22, 0) * mm, "construction": true});
            skLineSegment(sketch, "E147", {"start": v(-22, 0) * mm, "end": v(0, 0) * mm, "construction": true});
            skLineSegment(sketch, "E148.MirrorCS", {"start": v(-38.5, 11.5) * mm, "end": v(-31.5, 11.5) * mm});
            skLineSegment(sketch, "E149.MirrorCS", {"start": v(-34, 14) * mm, "end": v(-34, 18) * mm});
            skLineSegment(sketch, "E150.MirrorCS", {"start": v(-38.5, 18) * mm, "end": v(-38.5, 11.5) * mm});
            skLineSegment(sketch, "E151.MirrorCS", {"start": v(-31.5, 11.5) * mm, "end": v(-34, 14) * mm});
            skLineSegment(sketch, "E152.MirrorCS", {"start": v(-34, 18) * mm, "end": v(-38.5, 18) * mm});
            skLineSegment(sketch, "E153.MirrorCS", {"start": v(-12.5, -11.5) * mm, "end": v(-10, -14) * mm});
            skLineSegment(sketch, "E154.MirrorCS", {"start": v(-10, -14) * mm, "end": v(-10, -18) * mm});
            skLineSegment(sketch, "E155.MirrorCS", {"start": v(-10, -18) * mm, "end": v(-5.5, -18) * mm});
            skLineSegment(sketch, "E156.MirrorCS", {"start": v(-5.5, -18) * mm, "end": v(-5.5, -11.5) * mm});
            skLineSegment(sketch, "E157.MirrorCS", {"start": v(-5.5, -11.5) * mm, "end": v(-12.5, -11.5) * mm});
            skLineSegment(sketch, "E158.MirrorCS", {"start": v(-34, -14) * mm, "end": v(-34, -18) * mm});
            skLineSegment(sketch, "E159.MirrorCS", {"start": v(-38.5, -11.5) * mm, "end": v(-31.5, -11.5) * mm});
            skLineSegment(sketch, "E160.MirrorCS", {"start": v(-34, -18) * mm, "end": v(-38.5, -18) * mm});
            skLineSegment(sketch, "E161.MirrorCS", {"start": v(-31.5, -11.5) * mm, "end": v(-34, -14) * mm});
            skLineSegment(sketch, "E162.MirrorCS", {"start": v(-38.5, -18) * mm, "end": v(-38.5, -11.5) * mm});
            skSolve(sketch);
        }
        {
            var Q0;
            Q0 = qSketchRegion(id + "F30", true);
            var Q1;
            Q1=makeQuery(id+"F27.opExtrude","CAP_FACE",FACE,{"disambiguationData":[OSD([sQuery(id+"F26.wireOp",EDGE,"E119.bottom"),sQuery(id+"F26.wireOp",EDGE,"E119.top"),sQuery(id+"F26.wireOp",EDGE,"E119.left"),sQuery(id+"F26.wireOp",EDGE,"E119.right"),sQuery(id+"F26.wireOp",EDGE,"E120.0")])],"isStart":false});
            extrude(context, id + "F31", {"entities" : qUnion([Q0]), "operationType" : NewBodyOperationType.REMOVE, "endBound" : BoundingType.UP_TO_SURFACE, "oppositeDirection" : true, "endBoundEntityFace" : qUnion([Q1]), "depth" : 25 * mm});
        }
        {
            var Q0;
            Q0=makeQuery(id+"F31.boolean.opBoolean","MERGE",FACE,{"derivedFrom":[makeQuery(id+"F27.opExtrude","CAP_FACE",FACE,{"disambiguationData":[OSD([sQuery(id+"F26.wireOp",EDGE,"E119.bottom"),sQuery(id+"F26.wireOp",EDGE,"E119.top"),sQuery(id+"F26.wireOp",EDGE,"E119.left"),sQuery(id+"F26.wireOp",EDGE,"E119.right"),sQuery(id+"F26.wireOp",EDGE,"E120.0")])],"isStart":false})],"fromTools":[makeQuery(id+"F31.opExtrude","CAP_FACE",FACE,{"disambiguationData":[OSD([sQuery(id+"F30.wireOp",EDGE,"E141"),sQuery(id+"F30.wireOp",EDGE,"E142"),sQuery(id+"F30.wireOp",EDGE,"E143"),sQuery(id+"F30.wireOp",EDGE,"E144"),sQuery(id+"F30.wireOp",EDGE,"E145")])],"isStart":false}),makeQuery(id+"F31.opExtrude","CAP_FACE",FACE,{"disambiguationData":[OSD([sQuery(id+"F30.wireOp",EDGE,"E148.MirrorCS"),sQuery(id+"F30.wireOp",EDGE,"E149.MirrorCS"),sQuery(id+"F30.wireOp",EDGE,"E150.MirrorCS"),sQuery(id+"F30.wireOp",EDGE,"E151.MirrorCS"),sQuery(id+"F30.wireOp",EDGE,"E152.MirrorCS")])],"isStart":false}),makeQuery(id+"F31.opExtrude","CAP_FACE",FACE,{"disambiguationData":[OSD([sQuery(id+"F30.wireOp",EDGE,"E153.MirrorCS"),sQuery(id+"F30.wireOp",EDGE,"E154.MirrorCS"),sQuery(id+"F30.wireOp",EDGE,"E155.MirrorCS"),sQuery(id+"F30.wireOp",EDGE,"E156.MirrorCS"),sQuery(id+"F30.wireOp",EDGE,"E157.MirrorCS")])],"isStart":false}),makeQuery(id+"F31.opExtrude","CAP_FACE",FACE,{"disambiguationData":[OSD([sQuery(id+"F30.wireOp",EDGE,"E158.MirrorCS"),sQuery(id+"F30.wireOp",EDGE,"E159.MirrorCS"),sQuery(id+"F30.wireOp",EDGE,"E160.MirrorCS"),sQuery(id+"F30.wireOp",EDGE,"E161.MirrorCS"),sQuery(id+"F30.wireOp",EDGE,"E162.MirrorCS")])],"isStart":false})]});
            var sketch = newSketch(context, id + "F32", { "sketchPlane" : qUnion([Q0])});
            skCircle(sketch, "E163", {"center": v(0, 0) * mm, "radius": 4.5 * mm});
            skSolve(sketch);
        }
        {
            var Q0;
            Q0 = qSketchRegion(id + "F32", true);
            extrude(context, id + "F33", {"entities" : qUnion([Q0]), "operationType" : NewBodyOperationType.REMOVE, "oppositeDirection" : true, "depth" : 5 * mm, "hasSecondDirection" : true, "secondDirectionOppositeDirection" : false, "secondDirectionDepth" : 5 * mm});
        }
        {
            var Q0;
            Q0=makeQuery(id+"F29.opExtrude","SWEPT_FACE",FACE,{"disambiguationData":[OSD([sQuery(id+"F28.wireOp",EDGE,"E128")])]});
            var sketch = newSketch(context, id + "F34", { "sketchPlane" : qUnion([Q0])});
            skArc(sketch, "E164", {"start": v(-38.5, -11.3) * mm, "mid": v(-35.05, -15.16) * mm, "end": v(-30.72, -18) * mm});
            skPoint(sketch, "E164.centerSnap0", {"position": v(-22, 11.5) * mm});
            skArc(sketch, "E165", {"start": v(8.72, -18) * mm, "mid": v(13.05, -15.16) * mm, "end": v(16.5, -11.3) * mm});
            skLineSegment(sketch, "E166.0", {"start": v(-38.5, 18) * mm, "end": v(-38.5, 11.3) * mm});
            skLineSegment(sketch, "E167.0", {"start": v(-38.5, -11.3) * mm, "end": v(-38.5, -18) * mm});
            skLineSegment(sketch, "E168.0", {"start": v(16.5, -18) * mm, "end": v(8.72, -18) * mm});
            skLineSegment(sketch, "E169.0", {"start": v(16.5, 18) * mm, "end": v(8.72, 18) * mm});
            skLineSegment(sketch, "E170.0", {"start": v(16.5, 11.3) * mm, "end": v(16.5, -11.3) * mm});
            skLineSegment(sketch, "E171", {"start": v(-38.5, 18) * mm, "end": v(-30.72, 18) * mm});
            skLineSegment(sketch, "E172", {"start": v(-38.5, -18) * mm, "end": v(-30.72, -18) * mm});
            skArc(sketch, "E173.trimOffspring", {"start": v(-30.72, 18) * mm, "mid": v(-35.05, 15.16) * mm, "end": v(-38.5, 11.3) * mm});
            skArc(sketch, "E174.trimOffspring", {"start": v(16.5, 11.3) * mm, "mid": v(13.05, 15.16) * mm, "end": v(8.72, 18) * mm});
            skLineSegment(sketch, "E175", {"start": v(16.5, 18) * mm, "end": v(20.92, 18) * mm});
            skLineSegment(sketch, "E176", {"start": v(20.92, 18) * mm, "end": v(20.92, -18) * mm});
            skLineSegment(sketch, "E177", {"start": v(20.92, -18) * mm, "end": v(16.5, -18) * mm});
            skPoint(sketch, "E178.orphan", {"position": v(-38.5, 1.5) * mm});
            skPoint(sketch, "E179.orphan", {"position": v(-38.5, -1.5) * mm});
            skSolve(sketch);
        }
        {
            var Q0;
            Q0 = qSketchRegion(id + "F34", true);
            extrude(context, id + "F35", {"entities" : qUnion([Q0]), "operationType" : NewBodyOperationType.REMOVE, "oppositeDirection" : true, "depth" : 25 * mm});
        }
        {
            var Q0;
            Q0=makeQuery(id+"F29.opExtrude","SWEPT_FACE",FACE,{"disambiguationData":[OSD([sQuery(id+"F28.wireOp",EDGE,"E128")])]});
            var sketch = newSketch(context, id + "F36", { "sketchPlane" : qUnion([Q0])});
            skLineSegment(sketch, "E180", {"start": v(-22, 11.5) * mm, "end": v(-22, 0) * mm, "construction": true});
            skLineSegment(sketch, "E181", {"start": v(-22, 0) * mm, "end": v(0, 0) * mm, "construction": true});
            skArc(sketch, "E182.0", {"start": v(-30.72, 18) * mm, "mid": v(-32.4, 17.08) * mm, "end": v(-34, 16) * mm, "construction": true});
            skArc(sketch, "E183.0", {"start": v(-34, -16) * mm, "mid": v(-32.4, -17.08) * mm, "end": v(-30.72, -18) * mm, "construction": true});
            skArc(sketch, "E184.MirrorCS", {"start": v(-13.28, 18) * mm, "mid": v(-11.6, 17.08) * mm, "end": v(-10, 16) * mm});
            skArc(sketch, "E185.MirrorCS", {"start": v(-10, -16) * mm, "mid": v(-11.6, -17.08) * mm, "end": v(-13.28, -18) * mm});
            skLineSegment(sketch, "E186.0", {"start": v(-10, 16) * mm, "end": v(-10, 18) * mm});
            skLineSegment(sketch, "E187.0", {"start": v(-10, 18) * mm, "end": v(-13.28, 18) * mm});
            skLineSegment(sketch, "E188.0", {"start": v(-10, -16) * mm, "end": v(-10, -18) * mm});
            skLineSegment(sketch, "E189.0", {"start": v(-10, -18) * mm, "end": v(-13.28, -18) * mm});
            skPoint(sketch, "E190.orphan", {"position": v(-10, 14) * mm});
            skPoint(sketch, "E191.orphan", {"position": v(-10, -14) * mm});
            skSolve(sketch);
        }
        {
            var Q0;
            Q0 = qSketchRegion(id + "F36", true);
            var Q1;
            Q1=makeQuery(id+"F31.boolean.opBoolean","MERGE",FACE,{"derivedFrom":[makeQuery(id+"F27.opExtrude","CAP_FACE",FACE,{"disambiguationData":[OSD([sQuery(id+"F26.wireOp",EDGE,"E119.bottom"),sQuery(id+"F26.wireOp",EDGE,"E119.top"),sQuery(id+"F26.wireOp",EDGE,"E119.left"),sQuery(id+"F26.wireOp",EDGE,"E119.right"),sQuery(id+"F26.wireOp",EDGE,"E120.0")])],"isStart":false})],"fromTools":[makeQuery(id+"F31.opExtrude","CAP_FACE",FACE,{"disambiguationData":[OSD([sQuery(id+"F30.wireOp",EDGE,"E141"),sQuery(id+"F30.wireOp",EDGE,"E142"),sQuery(id+"F30.wireOp",EDGE,"E143"),sQuery(id+"F30.wireOp",EDGE,"E144"),sQuery(id+"F30.wireOp",EDGE,"E145")])],"isStart":false}),makeQuery(id+"F31.opExtrude","CAP_FACE",FACE,{"disambiguationData":[OSD([sQuery(id+"F30.wireOp",EDGE,"E148.MirrorCS"),sQuery(id+"F30.wireOp",EDGE,"E149.MirrorCS"),sQuery(id+"F30.wireOp",EDGE,"E150.MirrorCS"),sQuery(id+"F30.wireOp",EDGE,"E151.MirrorCS"),sQuery(id+"F30.wireOp",EDGE,"E152.MirrorCS")])],"isStart":false}),makeQuery(id+"F31.opExtrude","CAP_FACE",FACE,{"disambiguationData":[OSD([sQuery(id+"F30.wireOp",EDGE,"E153.MirrorCS"),sQuery(id+"F30.wireOp",EDGE,"E154.MirrorCS"),sQuery(id+"F30.wireOp",EDGE,"E155.MirrorCS"),sQuery(id+"F30.wireOp",EDGE,"E156.MirrorCS"),sQuery(id+"F30.wireOp",EDGE,"E157.MirrorCS")])],"isStart":false}),makeQuery(id+"F31.opExtrude","CAP_FACE",FACE,{"disambiguationData":[OSD([sQuery(id+"F30.wireOp",EDGE,"E158.MirrorCS"),sQuery(id+"F30.wireOp",EDGE,"E159.MirrorCS"),sQuery(id+"F30.wireOp",EDGE,"E160.MirrorCS"),sQuery(id+"F30.wireOp",EDGE,"E161.MirrorCS"),sQuery(id+"F30.wireOp",EDGE,"E162.MirrorCS")])],"isStart":false})]});
            extrude(context, id + "F37", {"entities" : qUnion([Q0]), "operationType" : NewBodyOperationType.REMOVE, "endBound" : BoundingType.UP_TO_SURFACE, "oppositeDirection" : true, "endBoundEntityFace" : qUnion([Q1]), "depth" : 25 * mm});
        }
        {
            var Q0;
            Q0=qCreatedBy(makeId("Top.planeOp"),FACE);
            var sketch = newSketch(context, id + "F38", { "sketchPlane" : qUnion([Q0])});
            skLineSegment(sketch, "E192.bottom", {"start": v(3.85, 60.52) * mm, "end": v(-28.15, 60.52) * mm});
            skLineSegment(sketch, "E192.top", {"start": v(3.85, 63.52) * mm, "end": v(-28.15, 63.52) * mm});
            skLineSegment(sketch, "E192.left", {"start": v(3.85, 60.52) * mm, "end": v(3.85, 63.52) * mm});
            skLineSegment(sketch, "E192.right", {"start": v(-28.15, 60.52) * mm, "end": v(-28.15, 63.52) * mm});
            skPoint(sketch, "E192.middle", {"position": v(-12.15, 62.02) * mm});
            skLineSegment(sketch, "E193.bottom", {"start": v(3.85, 66.52) * mm, "end": v(-28.15, 66.52) * mm});
            skLineSegment(sketch, "E193.top", {"start": v(3.85, 69.52) * mm, "end": v(-28.15, 69.52) * mm});
            skLineSegment(sketch, "E193.left", {"start": v(3.85, 66.52) * mm, "end": v(3.85, 69.52) * mm});
            skLineSegment(sketch, "E193.right", {"start": v(-28.15, 66.52) * mm, "end": v(-28.15, 69.52) * mm});
            skPoint(sketch, "E193.middle", {"position": v(-12.15, 68.02) * mm});
            skLineSegment(sketch, "E194", {"start": v(-12.15, 62.02) * mm, "end": v(-12.15, 68.02) * mm, "construction": true});
            skLineSegment(sketch, "E195.bottom", {"start": v(6.85, 72.52) * mm, "end": v(-31.15, 72.52) * mm});
            skLineSegment(sketch, "E195.top", {"start": v(6.85, 57.52) * mm, "end": v(-31.15, 57.52) * mm});
            skLineSegment(sketch, "E195.left", {"start": v(6.85, 72.52) * mm, "end": v(6.85, 57.52) * mm});
            skLineSegment(sketch, "E195.right", {"start": v(-31.15, 72.52) * mm, "end": v(-31.15, 57.52) * mm});
            skPoint(sketch, "E195.middle", {"position": v(-12.15, 65.02) * mm});
            skSolve(sketch);
        }
        {
            var Q0;
            Q0 = qSketchRegion(id + "F38", true);
            extrude(context, id + "F39", {"entities" : qUnion([Q0]), "depth" : 3 * mm});
        }
        {
            var Q0;
            Q0=makeQuery(id+"F39.opExtrude","SWEPT_EDGE",EDGE,{"disambiguationData":[OSD([sQuery(id+"F38.wireOp",EDGE,"E193.top"),sQuery(id+"F38.wireOp",EDGE,"E193.left")])]});
            var Q1;
            Q1=makeQuery(id+"F39.opExtrude","SWEPT_EDGE",EDGE,{"disambiguationData":[OSD([sQuery(id+"F38.wireOp",EDGE,"E192.top"),sQuery(id+"F38.wireOp",EDGE,"E192.left")])]});
            var Q2;
            Q2=makeQuery(id+"F39.opExtrude","SWEPT_EDGE",EDGE,{"disambiguationData":[OSD([sQuery(id+"F38.wireOp",EDGE,"E193.top"),sQuery(id+"F38.wireOp",EDGE,"E193.right")])]});
            var Q3;
            Q3=makeQuery(id+"F39.opExtrude","SWEPT_EDGE",EDGE,{"disambiguationData":[OSD([sQuery(id+"F38.wireOp",EDGE,"E192.top"),sQuery(id+"F38.wireOp",EDGE,"E192.right")])]});
            var Q4;
            Q4=makeQuery(id+"F39.opExtrude","SWEPT_EDGE",EDGE,{"disambiguationData":[OSD([sQuery(id+"F38.wireOp",EDGE,"E192.bottom"),sQuery(id+"F38.wireOp",EDGE,"E192.right")])]});
            var Q5;
            Q5=makeQuery(id+"F39.opExtrude","SWEPT_EDGE",EDGE,{"disambiguationData":[OSD([sQuery(id+"F38.wireOp",EDGE,"E193.bottom"),sQuery(id+"F38.wireOp",EDGE,"E193.right")])]});
            var Q6;
            Q6=makeQuery(id+"F39.opExtrude","SWEPT_EDGE",EDGE,{"disambiguationData":[OSD([sQuery(id+"F38.wireOp",EDGE,"E192.bottom"),sQuery(id+"F38.wireOp",EDGE,"E192.left")])]});
            var Q7;
            Q7=makeQuery(id+"F39.opExtrude","SWEPT_EDGE",EDGE,{"disambiguationData":[OSD([sQuery(id+"F38.wireOp",EDGE,"E193.bottom"),sQuery(id+"F38.wireOp",EDGE,"E193.left")])]});
            fillet(context, id + "F40", {"entities" : qUnion([Q0, Q1, Q2, Q3, Q4, Q5, Q6, Q7]), "radius" : 1 * mm, "tangentPropagation" : true, "allowEdgeOverflow" : false});
        }
        {
            var Q0;
            Q0=makeQuery(id+"F39.opExtrude","SWEPT_EDGE",EDGE,{"disambiguationData":[OSD([sQuery(id+"F38.wireOp",EDGE,"E195.top"),sQuery(id+"F38.wireOp",EDGE,"E195.left")])]});
            var Q1;
            Q1=makeQuery(id+"F39.opExtrude","SWEPT_EDGE",EDGE,{"disambiguationData":[OSD([sQuery(id+"F38.wireOp",EDGE,"E195.bottom"),sQuery(id+"F38.wireOp",EDGE,"E195.left")])]});
            var Q2;
            Q2=makeQuery(id+"F39.opExtrude","SWEPT_EDGE",EDGE,{"disambiguationData":[OSD([sQuery(id+"F38.wireOp",EDGE,"E195.top"),sQuery(id+"F38.wireOp",EDGE,"E195.right")])]});
            var Q3;
            Q3=makeQuery(id+"F39.opExtrude","SWEPT_EDGE",EDGE,{"disambiguationData":[OSD([sQuery(id+"F38.wireOp",EDGE,"E195.bottom"),sQuery(id+"F38.wireOp",EDGE,"E195.right")])]});
            fillet(context, id + "F41", {"entities" : qUnion([Q0, Q1, Q2, Q3]), "radius" : 5 * mm, "tangentPropagation" : true, "allowEdgeOverflow" : false});
        }
    });
